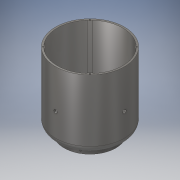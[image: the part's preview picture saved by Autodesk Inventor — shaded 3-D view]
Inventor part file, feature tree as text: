
AUTODESK INVENTOR PART (.ipt)
format: ipt  version: 2017 (Build 210142000, 142)  size: 273,408 bytes
history: native  units: in
note: dims shown in document units (in); Inventor stores cm internally (conversion verified against a paired STEP export)
features: sketch x7, pattern_circular x4, hole x3, extrude x3, plane x2, revolve x1, fillet x1
ambient origin geometry x8: Origin, YZ Plane, XZ Plane, XY Plane, X Axis, Y Axis, Z Axis, Center Point
bodies: Solid1 (feature_tree)
feature tree (21):
  revolve  "Revolution1"  [1 undecoded]
  fillet  "Fillet1"  Radius=1.0in
  plane  "Work Plane1"
  hole  "Hole1"  [1 undecoded]
  pattern_circular  "Circular Pattern1"  [2 undecoded]
  plane  "Work Plane2"
  hole  "Hole2"  [1 undecoded]
  pattern_circular  "Circular Pattern2"  [2 undecoded]
  extrude  "Extrusion1"  Depth=2.3622in TaperAngle=360.0deg
  extrude  "Extrusion2"  Depth=1.5748in TaperAngle=360.0deg
  extrude  "Extrusion3"  Depth=0.75in
  pattern_circular  "Circular Pattern3"  [2 undecoded]
  hole  "Hole7"  [1 undecoded]
  pattern_circular  "Circular Pattern4"  [2 undecoded]
  sketch  "Sketch1"  dims[d0=9.0in d1=5.0in d2=1.0in]
  sketch  "Sketch2"  dims[d3=4.366in d4=10.3219in]
  sketch  "Sketch3"  dims[d5=0.862in]
  sketch  "Sketch4"  dims[d6=3.5in]
  sketch  "Sketch5"  dims[d8=0.862in]
  sketch  "Sketch6"  dims[d16=0.5in]
  sketch  "Sketch11"  dims[d17=90.0deg d22=3.75in d23=0.125in d24=4.85in d25=0.196in d26=0.5in d27=0.375in d28=0.25in d29=0.5635in d30=0.75in d31=0.8108in d32=2.3622in d33=360.0deg d35=0.5in d36=0.75in d37=0.375in d38=0.25in d39=0.5635in d40=0.75in d41=0.8108in d42=1.5748in d43=360.0deg d45=0.75in d46=1.6875in d47=0.0in d48=9.5in d49=9.0in d50=0.0in d53=45.0deg d54=0.1694in d55=9.0in d56=0.0in d57=1.5748in d58=360.0deg d89=0.196in d90=0.5in d91=0.375in d92=0.25in d93=0.5635in d94=0.75in d95=0.8108in d96=1.5748in d97=360.0deg d67=1.0in d68=1.0in]
note: 12 required parameter values undecoded (feature->parameter linkage not recoverable at this tier; creation-order binding heuristic only, values carry confidence <= 0.55)